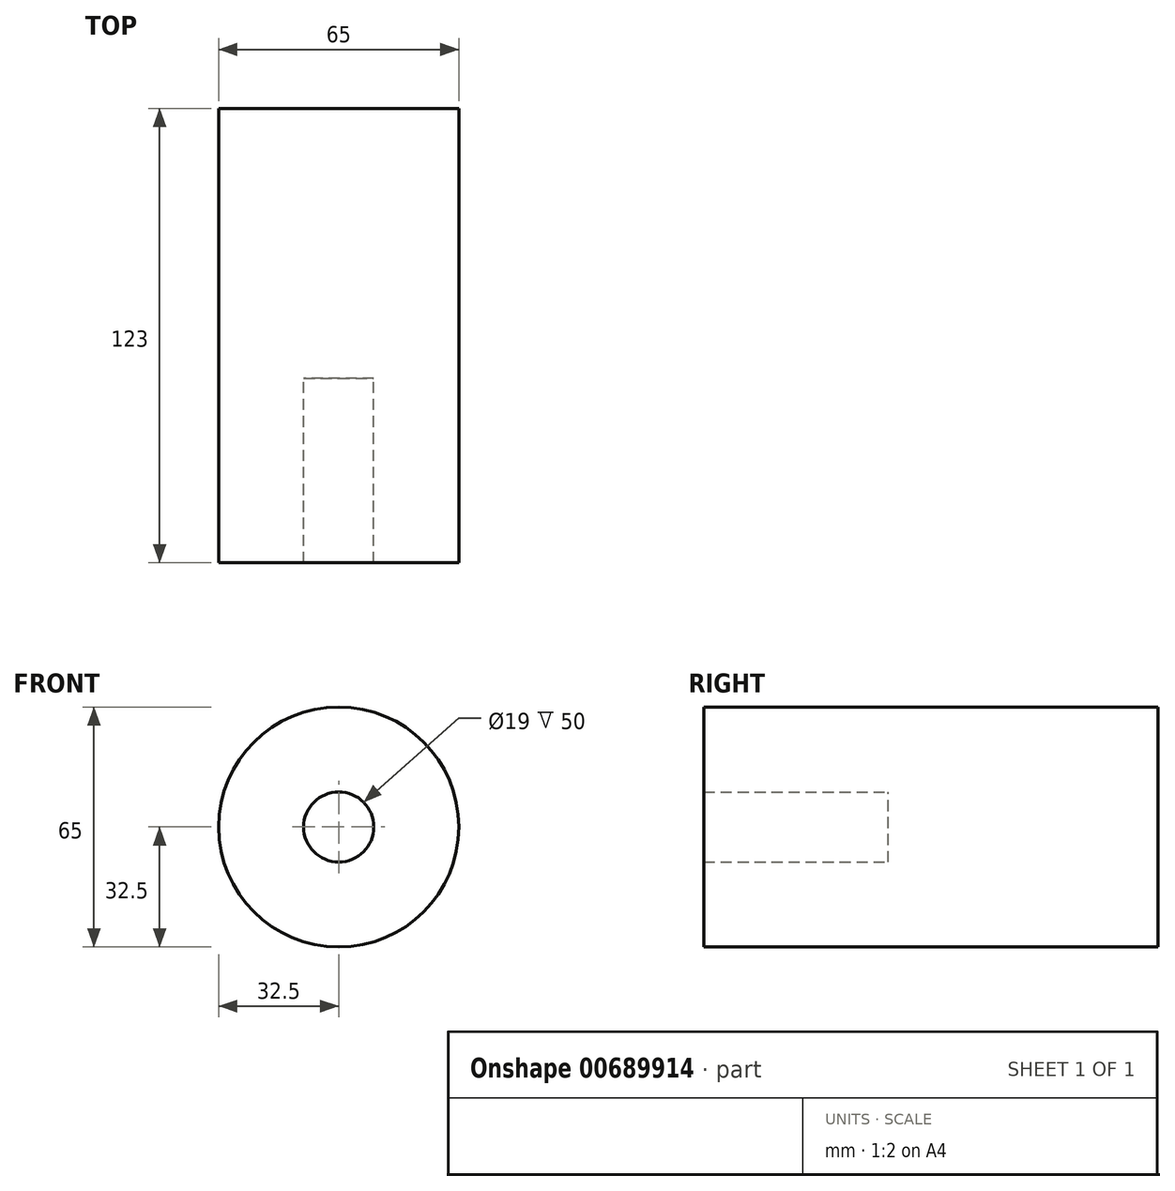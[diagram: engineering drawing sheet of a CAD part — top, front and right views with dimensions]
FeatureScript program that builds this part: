
annotation { "Feature Type Name" : "Feature", "Feature Type Description" : "" }
export const myFeature = defineFeature(function(context is Context, id is Id, definition is map)
    precondition{}
    {
        {
            var Q0;
            Q0=qCreatedBy(makeId("Front.planeOp"),FACE);
            var sketch = newSketch(context, id + "F0", { "sketchPlane" : qUnion([Q0])});
            skCircle(sketch, "E0", {"center": v(0, 0) * mm, "radius": 32.5 * mm});
            skCircle(sketch, "E1", {"center": v(0, 0) * mm, "radius": 9.5 * mm});
            skSolve(sketch);
        }
        {
            var Q0;
            Q0=makeQuery(id+"F0.imprint","IMPRINT",FACE,{"disambiguationData":[TD([[makeQuery(id+"F0.imprint","IMPRINT",EDGE,{"derivedFrom":sQuery(id+"F0.wireOp",EDGE,"E0")}),1.0]])]});
            var Q1;
            Q1=makeQuery(id+"F0.imprint","IMPRINT",FACE,{"disambiguationData":[TD([[makeQuery(id+"F0.imprint","IMPRINT",EDGE,{"derivedFrom":sQuery(id+"F0.wireOp",EDGE,"E0")}),1.0]])]});
            extrude(context, id + "F1", {"entities" : qUnion([Q0, Q1]), "depth" : 123 * mm, "offsetDistance" : 25 * mm});
        }
        {
            var Q0;
            Q0=qCreatedBy(makeId("Front.planeOp"),FACE);
            var sketch = newSketch(context, id + "F2", { "sketchPlane" : qUnion([Q0])});
            skCircle(sketch, "E2", {"center": v(0, 0) * mm, "radius": 9.5 * mm});
            skSolve(sketch);
        }
        {
            var Q0;
            Q0=makeQuery(id+"F2.imprint","IMPRINT",FACE,{"disambiguationData":[TD([[makeQuery(id+"F2.imprint","IMPRINT",EDGE,{"derivedFrom":sQuery(id+"F2.wireOp",EDGE,"E2")}),1.0]])]});
            extrude(context, id + "F3", {"entities" : qUnion([Q0]), "operationType" : NewBodyOperationType.ADD, "depth" : 73 * mm, "offsetDistance" : 25 * mm});
        }
    });
